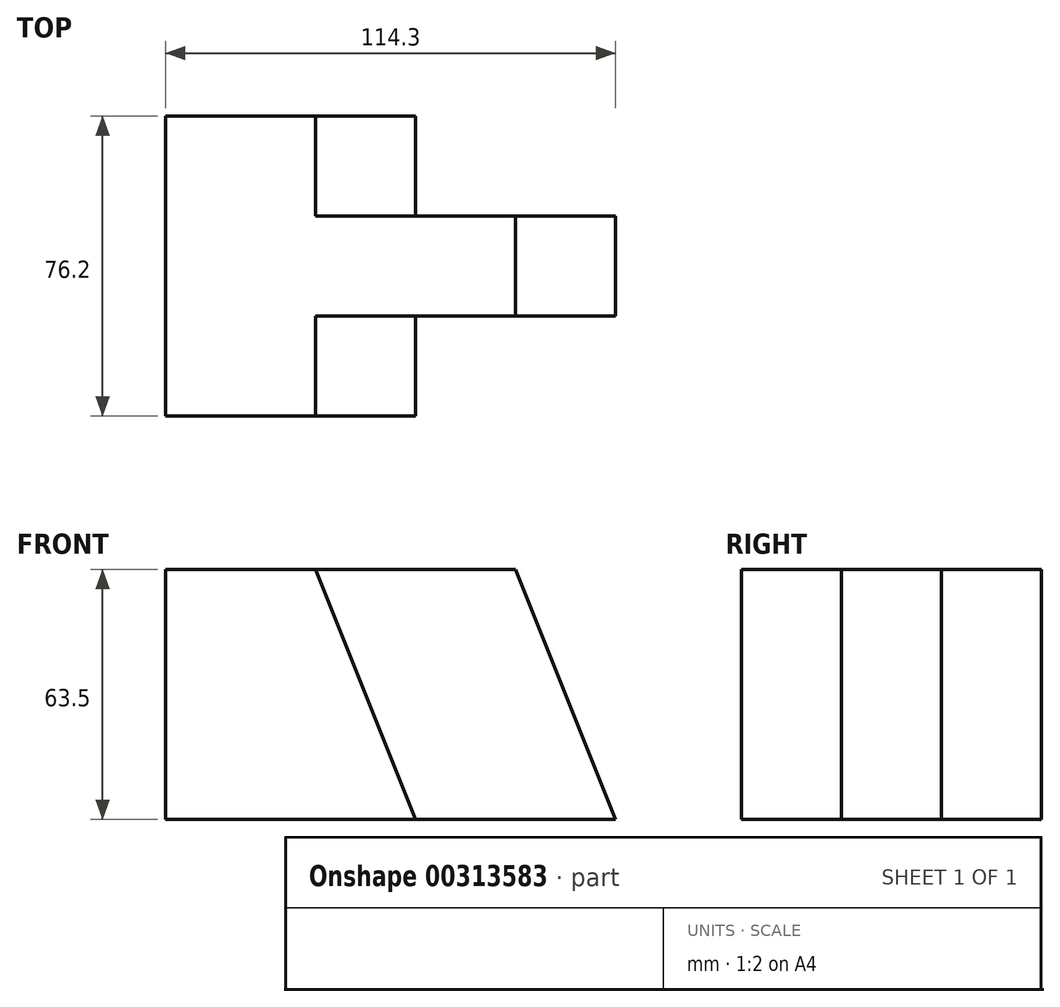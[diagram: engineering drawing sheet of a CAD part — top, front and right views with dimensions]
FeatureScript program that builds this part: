
annotation { "Feature Type Name" : "Feature", "Feature Type Description" : "" }
export const myFeature = defineFeature(function(context is Context, id is Id, definition is map)
    precondition{}
    {
        {
            var Q0;
            Q0=qCreatedBy(makeId("Front.planeOp"),FACE);
            var sketch = newSketch(context, id + "F0", { "sketchPlane" : qUnion([Q0])});
            skLineSegment(sketch, "E0", {"start": v(-23.12, -49.23) * mm, "end": v(40.38, -49.23) * mm});
            skLineSegment(sketch, "E1", {"start": v(-23.12, -49.23) * mm, "end": v(-23.12, 14.27) * mm});
            skLineSegment(sketch, "E2", {"start": v(-23.12, 14.27) * mm, "end": v(14.98, 14.27) * mm});
            skLineSegment(sketch, "E3", {"start": v(14.98, 14.27) * mm, "end": v(40.38, -49.23) * mm});
            skSolve(sketch);
        }
        {
            var Q0;
            Q0=makeQuery(id+"F0.imprint","IMPRINT",FACE,{"disambiguationData":[TD([[makeQuery(id+"F0.imprint","IMPRINT",EDGE,{"derivedFrom":sQuery(id+"F0.wireOp",EDGE,"E0")}),1.0]])]});
            extrude(context, id + "F1", {"entities" : qUnion([Q0]), "depth" : 76.2 * mm});
        }
        {
            var Q0;
            Q0=makeQuery(id+"F1.opExtrude","SWEPT_FACE",FACE,{"disambiguationData":[OSD([sQuery(id+"F0.wireOp",EDGE,"E1")])]});
            var sketch = newSketch(context, id + "F2", { "sketchPlane" : qUnion([Q0])});
            skLineSegment(sketch, "E4", {"start": v(25.4, 14.27) * mm, "end": v(25.4, -49.23) * mm});
            skLineSegment(sketch, "E5", {"start": v(25.4, -49.23) * mm, "end": v(50.8, -49.23) * mm});
            skLineSegment(sketch, "E6", {"start": v(50.8, -49.23) * mm, "end": v(50.8, 14.27) * mm});
            skLineSegment(sketch, "E7", {"start": v(50.8, 14.27) * mm, "end": v(25.4, 14.27) * mm});
            skSolve(sketch);
        }
        {
            var Q0;
            Q0=makeQuery(id+"F2.imprint","IMPRINT",FACE,{"disambiguationData":[TD([[makeQuery(id+"F2.imprint","IMPRINT",EDGE,{"derivedFrom":sQuery(id+"F2.wireOp",EDGE,"E4")}),1.0]])]});
            extrude(context, id + "F3", {"entities" : qUnion([Q0]), "operationType" : NewBodyOperationType.ADD, "oppositeDirection" : true, "depth" : 114.3 * mm});
        }
        {
            var Q0;
            Q0=makeQuery(id+"F3.opExtrude","SWEPT_FACE",FACE,{"disambiguationData":[OSD([sQuery(id+"F2.wireOp",EDGE,"E4")])]});
            var sketch = newSketch(context, id + "F4", { "sketchPlane" : qUnion([Q0])});
            skLineSegment(sketch, "E8", {"start": v(-65.78, 14.27) * mm, "end": v(-91.18, -49.23) * mm});
            skLineSegment(sketch, "E9", {"start": v(-91.18, -49.23) * mm, "end": v(-91.18, 14.27) * mm});
            skLineSegment(sketch, "E10", {"start": v(-91.18, 14.27) * mm, "end": v(-65.78, 14.27) * mm});
            skSolve(sketch);
        }
        {
            var Q0;
            Q0=makeQuery(id+"F4.imprint","IMPRINT",FACE,{"disambiguationData":[TD([[makeQuery(id+"F4.imprint","IMPRINT",EDGE,{"derivedFrom":sQuery(id+"F4.wireOp",EDGE,"E8")}),-1.0]])]});
            extrude(context, id + "F5", {"entities" : qUnion([Q0]), "operationType" : NewBodyOperationType.REMOVE, "oppositeDirection" : true, "depth" : 25.4 * mm});
        }
    });
